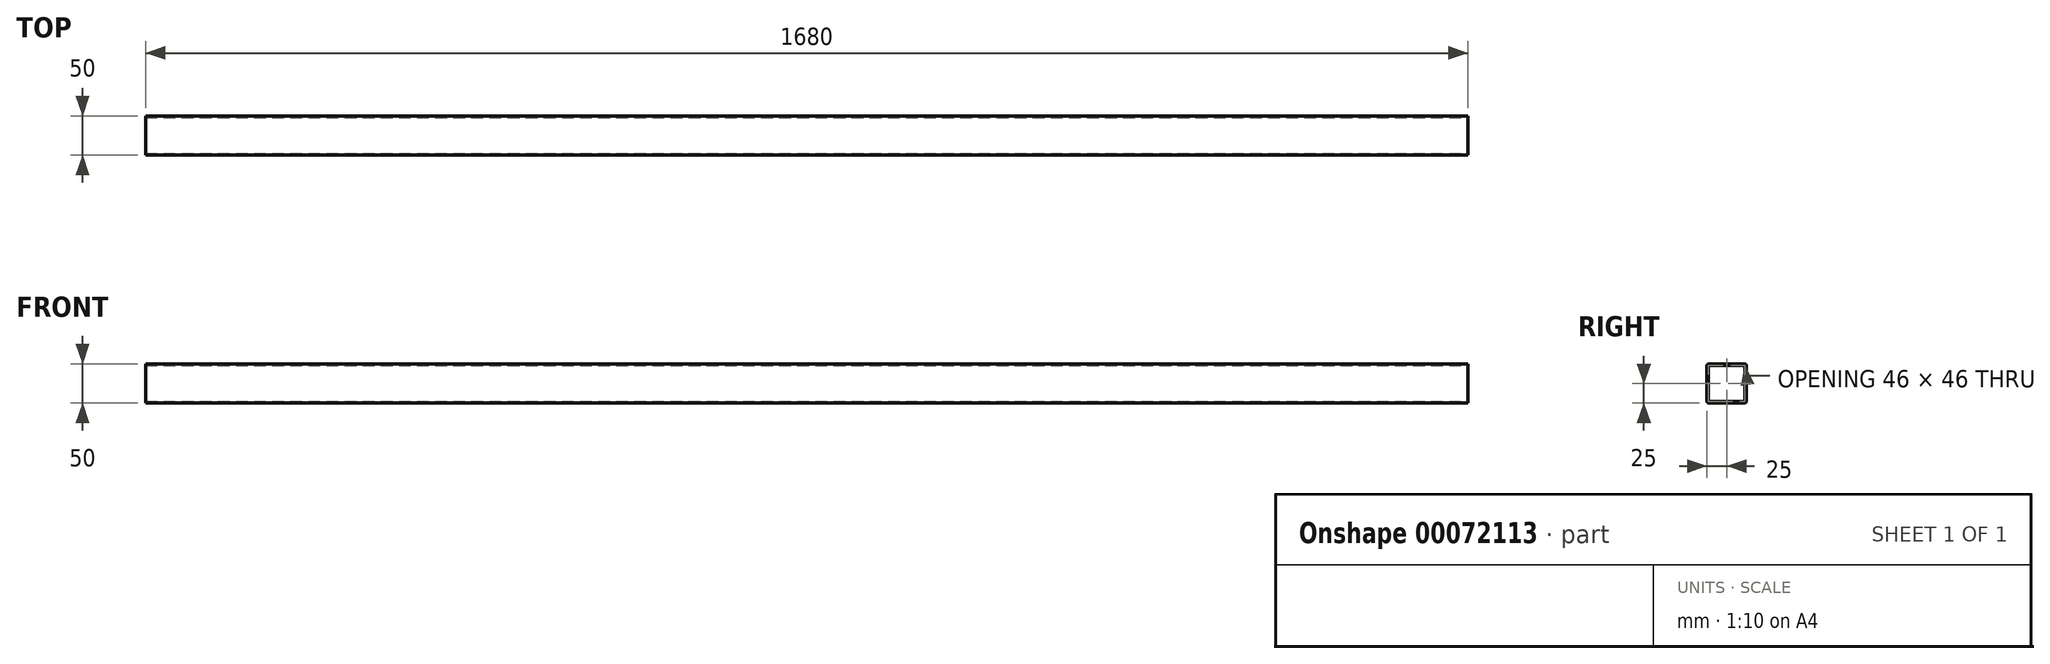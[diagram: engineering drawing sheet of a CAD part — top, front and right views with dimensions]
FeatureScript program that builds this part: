
annotation { "Feature Type Name" : "Feature", "Feature Type Description" : "" }
export const myFeature = defineFeature(function(context is Context, id is Id, definition is map)
    precondition{}
    {
        {
            var Q0;
            Q0=qCreatedBy(makeId("Top.planeOp"),FACE);
            var sketch = newSketch(context, id + "F0", { "sketchPlane" : qUnion([Q0])});
            skLineSegment(sketch, "E0.bottom", {"start": v(-54.16, 61.71) * mm, "end": v(-4.16, 61.71) * mm});
            skLineSegment(sketch, "E0.top", {"start": v(-54.16, 11.71) * mm, "end": v(-4.16, 11.71) * mm});
            skLineSegment(sketch, "E0.left", {"start": v(-54.16, 61.71) * mm, "end": v(-54.16, 11.71) * mm});
            skLineSegment(sketch, "E0.right", {"start": v(-4.16, 61.71) * mm, "end": v(-4.16, 11.71) * mm});
            skLineSegment(sketch, "E1.0", {"start": v(-52.16, 59.71) * mm, "end": v(-6.16, 59.71) * mm});
            skLineSegment(sketch, "E1.1", {"start": v(-52.16, 59.71) * mm, "end": v(-52.16, 13.71) * mm});
            skLineSegment(sketch, "E1.2", {"start": v(-52.16, 13.71) * mm, "end": v(-6.16, 13.71) * mm});
            skLineSegment(sketch, "E1.3", {"start": v(-6.16, 59.71) * mm, "end": v(-6.16, 13.71) * mm});
            skSolve(sketch);
        }
        {
            var Q0;
            Q0=makeQuery(id+"F0.imprint","IMPRINT",FACE,{"disambiguationData":[TD([[makeQuery(id+"F0.imprint","IMPRINT",EDGE,{"derivedFrom":sQuery(id+"F0.wireOp",EDGE,"E0.bottom")}),-1.0]])]});
            extrude(context, id + "F1", {"entities" : qUnion([Q0]), "depth" : 860 * mm});
        }
        {
            var Q0;
            Q0=makeQuery(id+"F1.opExtrude","SWEPT_EDGE",EDGE,{"disambiguationData":[OSD([sQuery(id+"F0.wireOp",EDGE,"E0.bottom"),sQuery(id+"F0.wireOp",EDGE,"E0.right")])]});
            var Q1;
            Q1=makeQuery(id+"F1.opExtrude","SWEPT_EDGE",EDGE,{"disambiguationData":[OSD([sQuery(id+"F0.wireOp",EDGE,"E0.bottom"),sQuery(id+"F0.wireOp",EDGE,"E0.left")])]});
            var Q2;
            Q2=makeQuery(id+"F1.opExtrude","SWEPT_EDGE",EDGE,{"disambiguationData":[OSD([sQuery(id+"F0.wireOp",EDGE,"E0.top"),sQuery(id+"F0.wireOp",EDGE,"E0.right")])]});
            var Q3;
            Q3=makeQuery(id+"F1.opExtrude","SWEPT_EDGE",EDGE,{"disambiguationData":[OSD([sQuery(id+"F0.wireOp",EDGE,"E0.top"),sQuery(id+"F0.wireOp",EDGE,"E0.left")])]});
            fillet(context, id + "F2", {"entities" : qUnion([Q0, Q1, Q2, Q3]), "radius" : 2.5 * mm, "tangentPropagation" : true, "allowEdgeOverflow" : false});
        }
        {
            var Q0;
            Q0=makeQuery(id+"F1.opExtrude","SWEPT_EDGE",EDGE,{"disambiguationData":[OSD([sQuery(id+"F0.wireOp",EDGE,"E1.0"),sQuery(id+"F0.wireOp",EDGE,"E1.3")])]});
            var Q1;
            Q1=makeQuery(id+"F1.opExtrude","SWEPT_EDGE",EDGE,{"disambiguationData":[OSD([sQuery(id+"F0.wireOp",EDGE,"E1.0"),sQuery(id+"F0.wireOp",EDGE,"E1.1")])]});
            var Q2;
            Q2=makeQuery(id+"F1.opExtrude","SWEPT_EDGE",EDGE,{"disambiguationData":[OSD([sQuery(id+"F0.wireOp",EDGE,"E1.1"),sQuery(id+"F0.wireOp",EDGE,"E1.2")])]});
            var Q3;
            Q3=makeQuery(id+"F1.opExtrude","SWEPT_EDGE",EDGE,{"disambiguationData":[OSD([sQuery(id+"F0.wireOp",EDGE,"E1.2"),sQuery(id+"F0.wireOp",EDGE,"E1.3")])]});
            fillet(context, id + "F3", {"entities" : qUnion([Q0, Q1, Q2, Q3]), "radius" : 2.5 * mm, "tangentPropagation" : true, "allowEdgeOverflow" : false});
        }
        {
            var Q0;
            Q0=makeQuery(id+"F1.opExtrude","SWEPT_BODY",BODY,{"disambiguationData":[OSD([sQuery(id+"F0.wireOp",EDGE,"E0.bottom"),sQuery(id+"F0.wireOp",EDGE,"E0.top"),sQuery(id+"F0.wireOp",EDGE,"E0.left"),sQuery(id+"F0.wireOp",EDGE,"E0.right"),sQuery(id+"F0.wireOp",EDGE,"E1.0"),sQuery(id+"F0.wireOp",EDGE,"E1.1"),sQuery(id+"F0.wireOp",EDGE,"E1.2"),sQuery(id+"F0.wireOp",EDGE,"E1.3")])]});
            transform(context, id + "F4", {"entities" : qUnion([Q0]), "transformType" : TransformType.TRANSLATION_3D, "dx" : 0 * mm, "dy" : 0 * mm, "dz" : 0 * mm, "makeCopy" : true});
        }
        {
            var Q0;
            Q0=makeQuery(id+"F4.opPattern","COPY",BODY,{"derivedFrom":makeQuery(id+"F1.opExtrude","SWEPT_BODY",BODY,{"disambiguationData":[OSD([sQuery(id+"F0.wireOp",EDGE,"E0.bottom"),sQuery(id+"F0.wireOp",EDGE,"E0.top"),sQuery(id+"F0.wireOp",EDGE,"E0.left"),sQuery(id+"F0.wireOp",EDGE,"E0.right"),sQuery(id+"F0.wireOp",EDGE,"E1.0"),sQuery(id+"F0.wireOp",EDGE,"E1.1"),sQuery(id+"F0.wireOp",EDGE,"E1.2"),sQuery(id+"F0.wireOp",EDGE,"E1.3")])]}),"instanceName":"1"});
            deleteBodies(context, id + "F5", {"entities" : qUnion([Q0])});
        }
        {
            var Q0;
            Q0=makeQuery(id+"F1.opExtrude","SWEPT_BODY",BODY,{"disambiguationData":[OSD([sQuery(id+"F0.wireOp",EDGE,"E0.bottom"),sQuery(id+"F0.wireOp",EDGE,"E0.top"),sQuery(id+"F0.wireOp",EDGE,"E0.left"),sQuery(id+"F0.wireOp",EDGE,"E0.right"),sQuery(id+"F0.wireOp",EDGE,"E1.0"),sQuery(id+"F0.wireOp",EDGE,"E1.1"),sQuery(id+"F0.wireOp",EDGE,"E1.2"),sQuery(id+"F0.wireOp",EDGE,"E1.3")])]});
            transform(context, id + "F6", {"entities" : qUnion([Q0]), "transformType" : TransformType.TRANSLATION_3D, "dx" : 0 * mm, "dy" : 0 * mm, "dz" : 0 * mm, "makeCopy" : true});
        }
        {
            var Q0;
            Q0=makeQuery(id+"F6.opPattern","COPY",BODY,{"derivedFrom":makeQuery(id+"F1.opExtrude","SWEPT_BODY",BODY,{"disambiguationData":[OSD([sQuery(id+"F0.wireOp",EDGE,"E0.bottom"),sQuery(id+"F0.wireOp",EDGE,"E0.top"),sQuery(id+"F0.wireOp",EDGE,"E0.left"),sQuery(id+"F0.wireOp",EDGE,"E0.right"),sQuery(id+"F0.wireOp",EDGE,"E1.0"),sQuery(id+"F0.wireOp",EDGE,"E1.1"),sQuery(id+"F0.wireOp",EDGE,"E1.2"),sQuery(id+"F0.wireOp",EDGE,"E1.3")])]}),"instanceName":"1"});
            deleteBodies(context, id + "F7", {"entities" : qUnion([Q0])});
        }
        {
            var Q0;
            Q0=makeQuery(id+"F1.opExtrude","CAP_FACE",FACE,{"disambiguationData":[OSD([sQuery(id+"F0.wireOp",EDGE,"E0.bottom"),sQuery(id+"F0.wireOp",EDGE,"E0.top"),sQuery(id+"F0.wireOp",EDGE,"E0.left"),sQuery(id+"F0.wireOp",EDGE,"E0.right"),sQuery(id+"F0.wireOp",EDGE,"E1.0"),sQuery(id+"F0.wireOp",EDGE,"E1.1"),sQuery(id+"F0.wireOp",EDGE,"E1.2"),sQuery(id+"F0.wireOp",EDGE,"E1.3")])],"isStart":false});
            extrude(context, id + "F8", {"entities" : qUnion([Q0]), "operationType" : NewBodyOperationType.ADD, "endBound" : BoundingType.SYMMETRIC, "depth" : 1640 * mm});
        }
        {
            var Q0;
            Q0=makeQuery(id+"F1.opExtrude","SWEPT_BODY",BODY,{"disambiguationData":[OSD([sQuery(id+"F0.wireOp",EDGE,"E0.bottom"),sQuery(id+"F0.wireOp",EDGE,"E0.top"),sQuery(id+"F0.wireOp",EDGE,"E0.left"),sQuery(id+"F0.wireOp",EDGE,"E0.right"),sQuery(id+"F0.wireOp",EDGE,"E1.0"),sQuery(id+"F0.wireOp",EDGE,"E1.1"),sQuery(id+"F0.wireOp",EDGE,"E1.2"),sQuery(id+"F0.wireOp",EDGE,"E1.3")])]});
            var Q1;
            Q1=sQuery(id+"F0.wireOp",EDGE,"E1.2");
            transform(context, id + "F9", {"entities" : qUnion([Q0]), "transformType" : TransformType.ROTATION, "transformAxis" : qUnion([Q1]), "angle" : 90 * degree, "makeCopy" : false});
        }
        {
            var Q0;
            Q0=makeQuery(id+"F1.opExtrude","SWEPT_BODY",BODY,{"disambiguationData":[OSD([sQuery(id+"F0.wireOp",EDGE,"E0.bottom"),sQuery(id+"F0.wireOp",EDGE,"E0.top"),sQuery(id+"F0.wireOp",EDGE,"E0.left"),sQuery(id+"F0.wireOp",EDGE,"E0.right"),sQuery(id+"F0.wireOp",EDGE,"E1.0"),sQuery(id+"F0.wireOp",EDGE,"E1.1"),sQuery(id+"F0.wireOp",EDGE,"E1.2"),sQuery(id+"F0.wireOp",EDGE,"E1.3")])]});
            var Q1;
            Q1=makeQuery(id+"F8.opExtrude","CAP_EDGE",EDGE,{"disambiguationData":[OSD([sQuery(id+"F0.wireOp",EDGE,"E0.right")])],"isStart":false});
            transform(context, id + "F10", {"entities" : qUnion([Q0]), "transformType" : TransformType.ROTATION, "transformAxis" : qUnion([Q1]), "angle" : 90 * degree, "makeCopy" : false});
        }
    });
